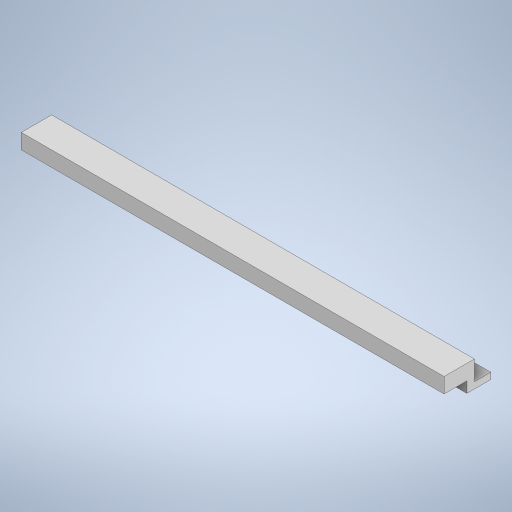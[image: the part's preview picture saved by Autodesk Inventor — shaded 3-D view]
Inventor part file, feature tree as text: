
AUTODESK INVENTOR PART (.ipt)
format: ipt  version: 2024 (Build 280153000, 153)  size: 234,496 bytes
history: native  units: mm
features: extrude x1, sketch x1
ambient origin geometry x8: Origin, YZ Plane, XZ Plane, XY Plane, X Axis, Y Axis, Z Axis, Center Point
bodies: Body1 (feature_tree)
feature tree (2):
  extrude  "Estrusione2"  Depth=390.0mm TaperAngle=0.0deg
  sketch  "Schizzo1"
